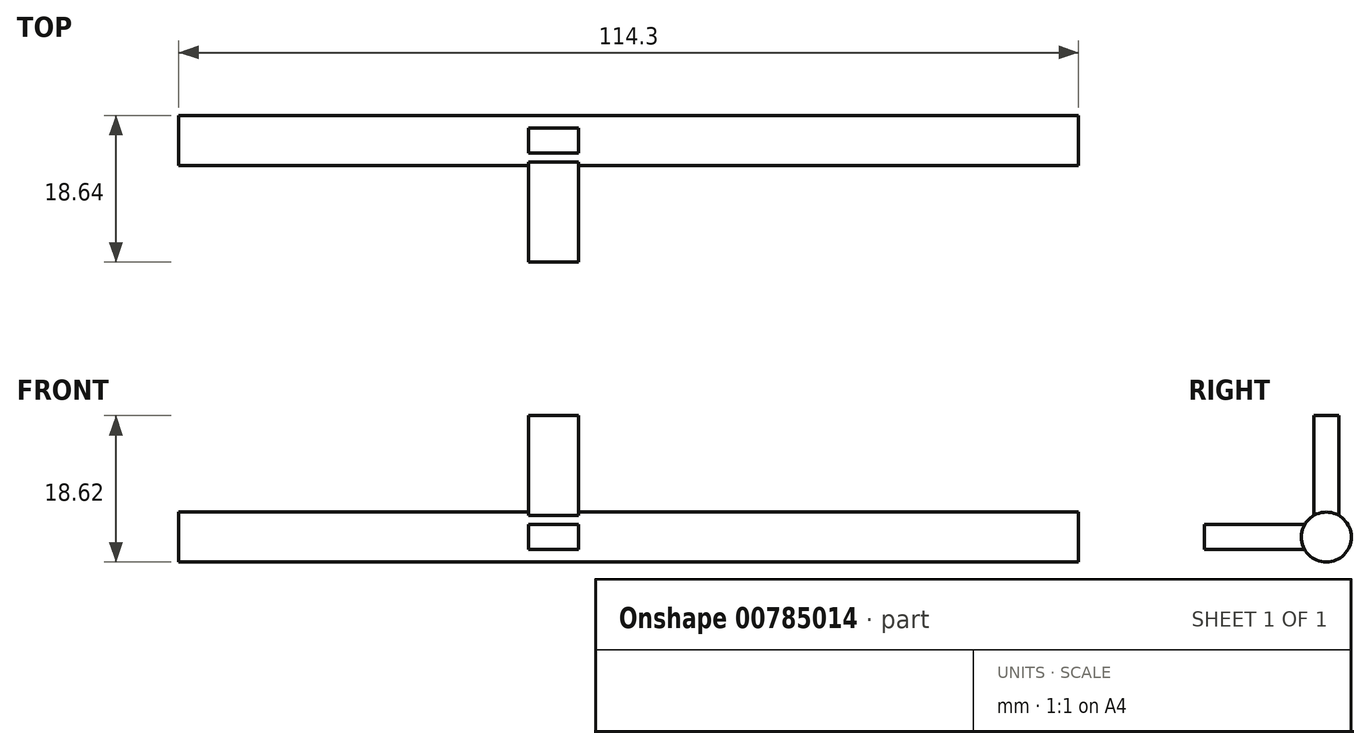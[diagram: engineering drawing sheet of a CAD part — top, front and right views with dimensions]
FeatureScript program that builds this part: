
annotation { "Feature Type Name" : "Feature", "Feature Type Description" : "" }
export const myFeature = defineFeature(function(context is Context, id is Id, definition is map)
    precondition{}
    {
        {
            var Q0;
            Q0=qCreatedBy(makeId("Right.planeOp"),FACE);
            var sketch = newSketch(context, id + "F0", { "sketchPlane" : qUnion([Q0])});
            skCircle(sketch, "E0", {"center": v(0, 0) * mm, "radius": 3.17 * mm});
            skSolve(sketch);
        }
        {
            var Q0;
            Q0=makeQuery(id+"F0.imprint","IMPRINT",FACE,{"disambiguationData":[TD([[makeQuery(id+"F0.imprint","IMPRINT",EDGE,{"derivedFrom":sQuery(id+"F0.wireOp",EDGE,"E0")}),1.0]])]});
            extrude(context, id + "F1", {"entities" : qUnion([Q0]), "depth" : 114.3 * mm, "offsetDistance" : 25.4 * mm});
        }
        {
            var Q0;
            Q0=makeQuery(id+"F1.opExtrude","CAP_FACE",FACE,{"disambiguationData":[OSD([sQuery(id+"F0.wireOp",EDGE,"E0")])],"isStart":true});
            var sketch = newSketch(context, id + "F2", { "sketchPlane" : qUnion([Q0])});
            skLineSegment(sketch, "E1.bottom", {"start": v(2.75, 1.59) * mm, "end": v(15.45, 1.59) * mm});
            skLineSegment(sketch, "E1.top", {"start": v(2.75, -1.59) * mm, "end": v(15.45, -1.59) * mm});
            skLineSegment(sketch, "E1.left", {"start": v(2.75, 1.59) * mm, "end": v(2.75, -1.59) * mm});
            skLineSegment(sketch, "E1.right", {"start": v(15.45, 1.59) * mm, "end": v(15.45, -1.59) * mm});
            skLineSegment(sketch, "E2.bottom", {"start": v(-1.59, 2.75) * mm, "end": v(1.59, 2.75) * mm});
            skLineSegment(sketch, "E2.top", {"start": v(-1.59, 15.45) * mm, "end": v(1.59, 15.45) * mm});
            skLineSegment(sketch, "E2.left", {"start": v(-1.59, 2.75) * mm, "end": v(-1.59, 15.45) * mm});
            skLineSegment(sketch, "E2.right", {"start": v(1.59, 2.75) * mm, "end": v(1.59, 15.45) * mm});
            skCircle(sketch, "E3", {"center": v(0, 0) * mm, "radius": 3.17 * mm});
            skSolve(sketch);
        }
        {
            var Q0;
            Q0=makeQuery(id+"F1.opExtrude","CAP_FACE",FACE,{"disambiguationData":[OSD([sQuery(id+"F0.wireOp",EDGE,"E0")])],"isStart":true});
            cPlane(context, id + "F3", {"entities" : qUnion([Q0]), "cplaneType" : CPlaneType.OFFSET, "offset" : 44.45 * mm, "oppositeDirection" : true, "width" : 152.4 * mm, "height" : 152.4 * mm});
        }
        {
            var Q0;
            Q0=qCreatedBy(id+"F3.planeOp",FACE);
            var sketch = newSketch(context, id + "F4", { "sketchPlane" : qUnion([Q0])});
            skLineSegment(sketch, "E4.bottom", {"start": v(2.76, 1.58) * mm, "end": v(15.46, 1.58) * mm});
            skLineSegment(sketch, "E4.top", {"start": v(2.76, -1.6) * mm, "end": v(15.46, -1.6) * mm});
            skLineSegment(sketch, "E4.left", {"start": v(2.76, 1.58) * mm, "end": v(2.76, -1.6) * mm});
            skLineSegment(sketch, "E4.right", {"start": v(15.46, 1.58) * mm, "end": v(15.46, -1.6) * mm});
            skLineSegment(sketch, "E5.bottom", {"start": v(-1.58, 2.74) * mm, "end": v(1.6, 2.74) * mm});
            skLineSegment(sketch, "E5.top", {"start": v(-1.58, 15.44) * mm, "end": v(1.6, 15.44) * mm});
            skLineSegment(sketch, "E5.left", {"start": v(-1.58, 2.74) * mm, "end": v(-1.58, 15.44) * mm});
            skLineSegment(sketch, "E5.right", {"start": v(1.6, 2.74) * mm, "end": v(1.6, 15.44) * mm});
            skCircle(sketch, "E6", {"center": v(0, 0) * mm, "radius": 3.17 * mm});
            skSolve(sketch);
        }
        {
            var Q0;
            {var subQ5=sQuery(id+"F4.wireOp",EDGE,"E4.bottom");Q0=makeQuery(id+"F4.imprint","IMPRINT",FACE,{"disambiguationData":[TD([[makeQuery(id+"F4.imprint","IMPRINT",EDGE,{"derivedFrom":subQ5}),-1.0]])]});}
            var Q1;
            {var subQ2=sQuery(id+"F4.wireOp",EDGE,"E5.top");Q1=makeQuery(id+"F4.imprint","IMPRINT",FACE,{"disambiguationData":[TD([[makeQuery(id+"F4.imprint","IMPRINT",EDGE,{"derivedFrom":subQ2}),-1.0]])]});}
            extrude(context, id + "F5", {"entities" : qUnion([Q0, Q1]), "operationType" : NewBodyOperationType.ADD, "oppositeDirection" : true, "depth" : 6.35 * mm, "offsetDistance" : 25.4 * mm});
        }
    });
